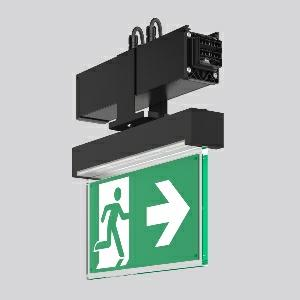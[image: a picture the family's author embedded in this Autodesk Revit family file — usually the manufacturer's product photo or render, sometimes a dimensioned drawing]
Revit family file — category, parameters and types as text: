
# Revit family: linedo_module_rz_9503rz_763_430_030_4ac7
name_source: partatom
category: Lighting Fixtures
units: mm (PartAtom-declared; Revit-internal decimal feet)

## family parameters
Cut with Voids When Loaded = No
Host = Face
Light Source = No
Part Type = Normal
Room Calculation Point = No
Round Connector Dimension = Use Diameter
Shared = No

## types (1)
- LINEDO Module RZ
    Apparent Load = 0 VA
    Default Elevation = 1800 mm
    Description = LINEDO, black, on/off
Continuous line luminaire, L 336 B 62 H 343, SBS, 3 h, automatischer Selbsttest
    Height = 343 mm
    Lamp = 0 x
    Length = 336 mm
    Luminous efficacy = 0 lm/W
    Manufacturer = RZB
    ModVariant = No
    Model = 9503RZ.763.430.030
    Mounting Place = Ceiling
    Mounting Type = Surface mounted
    Number of Poles = 1
    OnlyDefault = Yes
    Power Factor = 1
    Product Name = LINEDO Module RZ
    Product group = Continuous line luminaire system Linedo IP 54
    ProductGroupID = 314
    Protection Class = Protection class I
    Protection Degree = IP 54
    RLX_Detail_Level = 1
    RLX_Emergency_Light_Flux = 0 lm
    RLX_Emergency_Type = 0
    RLX_Emergency_Type_DB = No
    RlxData = <blob elided: 39861 chars, md5=3b2dc6a8>
    Standby Power = 0 W
    System Light Flux = 0 lm
    System Power = 0 W
    Type Comments = Product without accessories
    Type Image = 9503rz.763.434.030.jpg
    URL = http://relux.com
    VarID = ---
    Voltage = 0 V
    Weight = 0.00 kg
    Width = 62 mm  [stored 0.203412 ft]

note: [stored X ft] marks values corroborated as IEEE doubles in the binary element streams (Revit-internal decimal feet)

## geometry (parser evidence)
native form markers: Blend x4, Sweep x12
no freeform markers — native parametric forms only
